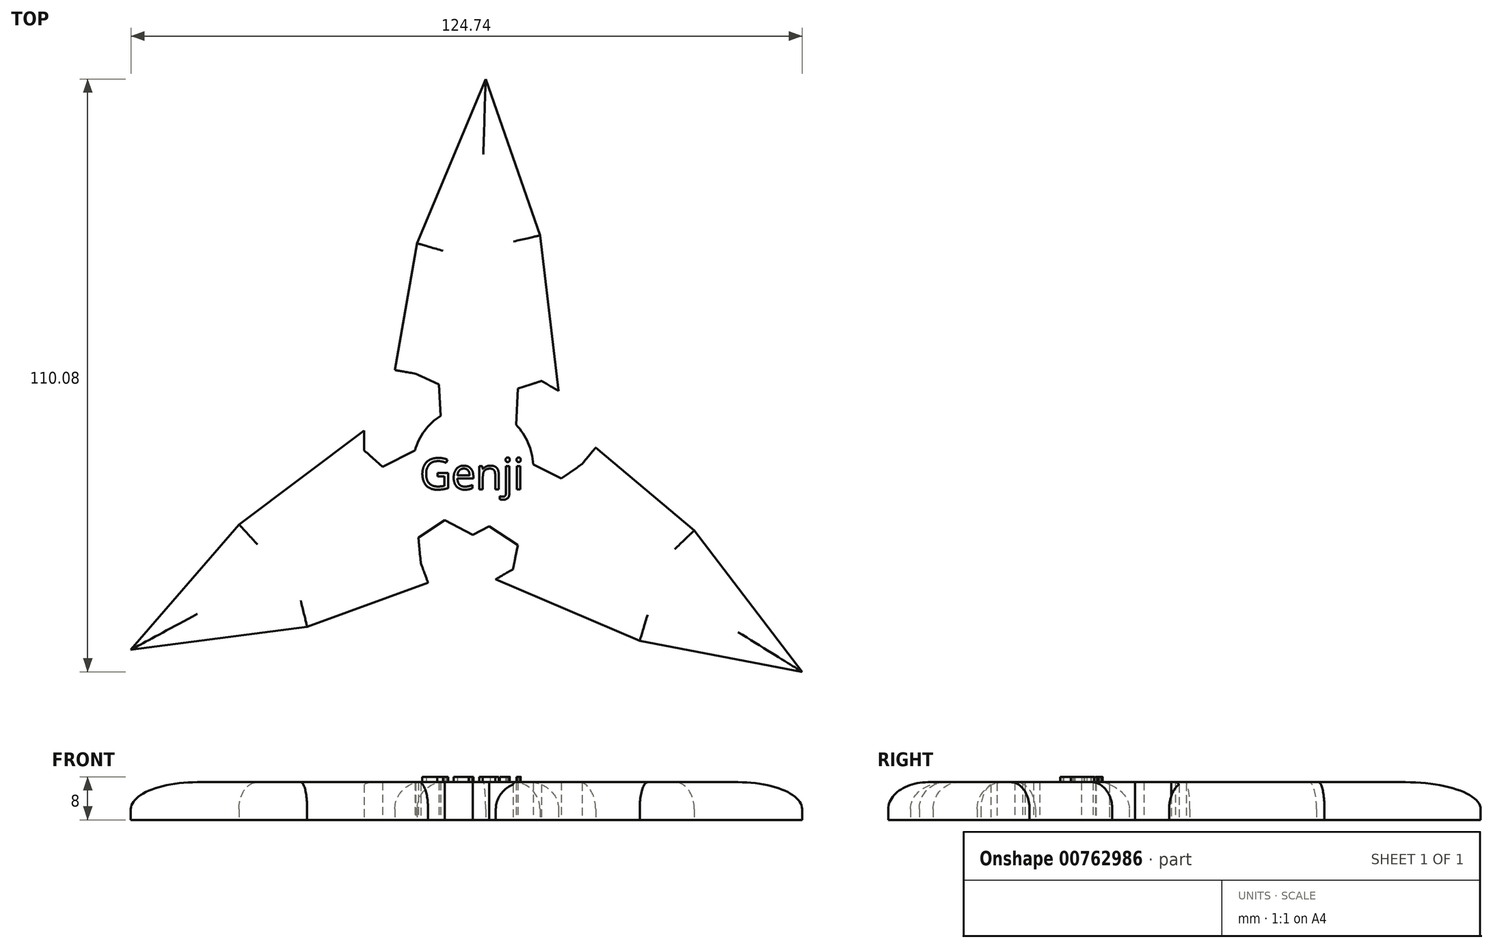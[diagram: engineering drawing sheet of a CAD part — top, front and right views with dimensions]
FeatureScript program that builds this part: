
annotation { "Feature Type Name" : "Feature", "Feature Type Description" : "" }
export const myFeature = defineFeature(function(context is Context, id is Id, definition is map)
    precondition{}
    {
        {
            var Q0;
            Q0=qCreatedBy(makeId("Top.planeOp"),FACE);
            var sketch = newSketch(context, id + "F0", { "sketchPlane" : qUnion([Q0])});
            skCircle(sketch, "E0", {"center": v(0, 0) * mm, "radius": 11.2 * mm});
            skLineSegment(sketch, "E1", {"start": v(-7.42, 8.39) * mm, "end": v(-10.77, 3.06) * mm});
            skLineSegment(sketch, "E2", {"start": v(-10.77, 3.06) * mm, "end": v(-16.78, 0) * mm});
            skLineSegment(sketch, "E3", {"start": v(-16.78, 0) * mm, "end": v(-20.2, 3.06) * mm});
            skLineSegment(sketch, "E4", {"start": v(-20.2, 3.06) * mm, "end": v(-20.2, 6.74) * mm});
            skLineSegment(sketch, "E5", {"start": v(-20.2, 6.74) * mm, "end": v(-43.47, -10.7) * mm});
            skLineSegment(sketch, "E6", {"start": v(-43.47, -10.7) * mm, "end": v(-63.55, -33.96) * mm});
            skLineSegment(sketch, "E7", {"start": v(-63.55, -33.96) * mm, "end": v(-30.79, -29.73) * mm});
            skLineSegment(sketch, "E8", {"start": v(-30.79, -29.73) * mm, "end": v(-8.32, -21.54) * mm});
            skLineSegment(sketch, "E9", {"start": v(-8.32, -21.54) * mm, "end": v(-9.67, -17.85) * mm});
            skLineSegment(sketch, "E10", {"start": v(-9.67, -17.85) * mm, "end": v(-10.09, -13.12) * mm});
            skLineSegment(sketch, "E11", {"start": v(-10.09, -13.12) * mm, "end": v(-5.2, -9.92) * mm});
            skLineSegment(sketch, "E12", {"start": v(-5.2, -9.92) * mm, "end": v(0, -12.64) * mm});
            skLineSegment(sketch, "E13", {"start": v(0, -12.64) * mm, "end": v(5.2, -9.92) * mm});
            skLineSegment(sketch, "E14.1.0", {"start": v(4.26, -20.86) * mm, "end": v(31, -32.3) * mm});
            skLineSegment(sketch, "E14.1.1", {"start": v(31, -32.3) * mm, "end": v(61.19, -38.06) * mm});
            skLineSegment(sketch, "E14.1.2", {"start": v(61.19, -38.06) * mm, "end": v(41.14, -11.8) * mm});
            skLineSegment(sketch, "E14.1.3", {"start": v(41.14, -11.8) * mm, "end": v(22.81, 3.56) * mm});
            skLineSegment(sketch, "E14.1.4", {"start": v(22.81, 3.56) * mm, "end": v(20.3, 0.55) * mm});
            skLineSegment(sketch, "E14.1.5", {"start": v(20.3, 0.55) * mm, "end": v(16.4, -2.18) * mm});
            skLineSegment(sketch, "E14.1.6", {"start": v(16.4, -2.18) * mm, "end": v(11.2, 0.46) * mm});
            skLineSegment(sketch, "E14.1.7", {"start": v(7.45, -19.02) * mm, "end": v(4.26, -20.86) * mm});
            skLineSegment(sketch, "E14.1.8", {"start": v(8.4, -14.53) * mm, "end": v(7.45, -19.02) * mm});
            skLineSegment(sketch, "E14.1.9", {"start": v(2.74, -10.86) * mm, "end": v(8.4, -14.53) * mm});
            skLineSegment(sketch, "E14.2.0", {"start": v(15.93, 14.12) * mm, "end": v(12.47, 43) * mm});
            skLineSegment(sketch, "E14.2.1", {"start": v(12.47, 43) * mm, "end": v(2.37, 72.02) * mm});
            skLineSegment(sketch, "E14.2.2", {"start": v(2.37, 72.02) * mm, "end": v(-10.35, 41.53) * mm});
            skLineSegment(sketch, "E14.2.3", {"start": v(-10.35, 41.53) * mm, "end": v(-14.49, 17.98) * mm});
            skLineSegment(sketch, "E14.2.4", {"start": v(-14.49, 17.98) * mm, "end": v(-10.62, 17.3) * mm});
            skLineSegment(sketch, "E14.2.5", {"start": v(-10.62, 17.3) * mm, "end": v(-6.32, 15.3) * mm});
            skLineSegment(sketch, "E14.2.6", {"start": v(-6.32, 15.3) * mm, "end": v(-6, 9.46) * mm});
            skLineSegment(sketch, "E14.2.7", {"start": v(12.74, 15.96) * mm, "end": v(15.93, 14.12) * mm});
            skLineSegment(sketch, "E14.2.8", {"start": v(8.4, 14.53) * mm, "end": v(12.74, 15.96) * mm});
            skLineSegment(sketch, "E14.2.9", {"start": v(8.04, 7.8) * mm, "end": v(8.4, 14.53) * mm});
            skLineSegment(sketch, "E15", {"start": v(-26.7, 1.86) * mm, "end": v(-29.22, -12.7) * mm});
            skPoint(sketch, "E15.endSnap0", {"position": v(5.56, -12.7) * mm});
            skLineSegment(sketch, "E16", {"start": v(-29.22, -12.7) * mm, "end": v(-13, -23.24) * mm});
            skLineSegment(sketch, "E17", {"start": v(-31.83, -1.98) * mm, "end": v(-57.12, -30.65) * mm});
            skLineSegment(sketch, "E18", {"start": v(-57.12, -30.65) * mm, "end": v(-16.88, -24.66) * mm});
            skLineSegment(sketch, "E19.1.0", {"start": v(17.63, -26.58) * mm, "end": v(55.1, -34.14) * mm});
            skLineSegment(sketch, "E19.1.1", {"start": v(55.1, -34.14) * mm, "end": v(29.8, -2.3) * mm});
            skLineSegment(sketch, "E19.1.2", {"start": v(25.6, -18.95) * mm, "end": v(26.62, 0.37) * mm});
            skLineSegment(sketch, "E19.1.3", {"start": v(11.74, -24.05) * mm, "end": v(25.6, -18.95) * mm});
            skLineSegment(sketch, "E19.2.0", {"start": v(14.2, 28.56) * mm, "end": v(2.01, 64.79) * mm});
            skLineSegment(sketch, "E19.2.1", {"start": v(2.01, 64.79) * mm, "end": v(-12.91, 26.95) * mm});
            skLineSegment(sketch, "E19.2.2", {"start": v(3.61, 31.65) * mm, "end": v(-13.63, 22.87) * mm});
            skLineSegment(sketch, "E19.2.3", {"start": v(14.96, 22.2) * mm, "end": v(3.61, 31.65) * mm});
            skLineSegment(sketch, "E20", {"start": v(8.04, 7.8) * mm, "end": v(11.2, 0.46) * mm});
            skSolve(sketch);
        }
        {
            var Q0;
            Q0 = qSketchRegion(id + "F0", true);
            extrude(context, id + "F1", {"entities" : qUnion([Q0]), "depth" : 7 * mm, "offsetDistance" : 25 * mm});
        }
        {
            var Q0;
            Q0=makeQuery(id+"F1.opExtrude","CAP_EDGE",EDGE,{"disambiguationData":[OSD([sQuery(id+"F0.wireOp",EDGE,"E14.2.3")])],"isStart":false});
            var Q1;
            Q1=makeQuery(id+"F1.opExtrude","CAP_EDGE",EDGE,{"disambiguationData":[OSD([sQuery(id+"F0.wireOp",EDGE,"E14.2.2")])],"isStart":false});
            var Q2;
            Q2=makeQuery(id+"F1.opExtrude","CAP_EDGE",EDGE,{"disambiguationData":[OSD([sQuery(id+"F0.wireOp",EDGE,"E14.2.0")])],"isStart":false});
            var Q3;
            Q3=makeQuery(id+"F1.opExtrude","CAP_EDGE",EDGE,{"disambiguationData":[OSD([sQuery(id+"F0.wireOp",EDGE,"E14.2.1")])],"isStart":false});
            var Q4;
            Q4=makeQuery(id+"F1.opExtrude","CAP_EDGE",EDGE,{"disambiguationData":[OSD([sQuery(id+"F0.wireOp",EDGE,"E5")])],"isStart":false});
            var Q5;
            Q5=makeQuery(id+"F1.opExtrude","CAP_EDGE",EDGE,{"disambiguationData":[OSD([sQuery(id+"F0.wireOp",EDGE,"E6")])],"isStart":false});
            var Q6;
            Q6=makeQuery(id+"F1.opExtrude","CAP_EDGE",EDGE,{"disambiguationData":[OSD([sQuery(id+"F0.wireOp",EDGE,"E14.1.0")])],"isStart":false});
            var Q7;
            Q7=makeQuery(id+"F1.opExtrude","CAP_EDGE",EDGE,{"disambiguationData":[OSD([sQuery(id+"F0.wireOp",EDGE,"E14.1.1")])],"isStart":false});
            var Q8;
            Q8=makeQuery(id+"F1.opExtrude","CAP_EDGE",EDGE,{"disambiguationData":[OSD([sQuery(id+"F0.wireOp",EDGE,"E14.1.3")])],"isStart":false});
            var Q9;
            Q9=makeQuery(id+"F1.opExtrude","CAP_EDGE",EDGE,{"disambiguationData":[OSD([sQuery(id+"F0.wireOp",EDGE,"E14.1.2")])],"isStart":false});
            var Q10;
            Q10=makeQuery(id+"F1.opExtrude","CAP_EDGE",EDGE,{"disambiguationData":[OSD([sQuery(id+"F0.wireOp",EDGE,"E7")])],"isStart":false});
            var Q11;
            Q11=makeQuery(id+"F1.opExtrude","CAP_EDGE",EDGE,{"disambiguationData":[OSD([sQuery(id+"F0.wireOp",EDGE,"E8")])],"isStart":false});
            fillet(context, id + "F2", {"entities" : qUnion([Q0, Q1, Q2, Q3, Q4, Q5, Q6, Q7, Q8, Q9, Q10, Q11]), "radius" : 5 * mm, "tangentPropagation" : true, "allowEdgeOverflow" : false});
        }
        {
            var Q0;
            Q0=makeQuery(id+"F1.opExtrude","CAP_FACE",FACE,{"disambiguationData":[OSD([sQuery(id+"F0.wireOp",EDGE,"E0"),sQuery(id+"F0.wireOp",EDGE,"E2"),sQuery(id+"F0.wireOp",EDGE,"E3"),sQuery(id+"F0.wireOp",EDGE,"E4"),sQuery(id+"F0.wireOp",EDGE,"E5"),sQuery(id+"F0.wireOp",EDGE,"E6"),sQuery(id+"F0.wireOp",EDGE,"E7"),sQuery(id+"F0.wireOp",EDGE,"E8"),sQuery(id+"F0.wireOp",EDGE,"E9"),sQuery(id+"F0.wireOp",EDGE,"E10"),sQuery(id+"F0.wireOp",EDGE,"E11"),sQuery(id+"F0.wireOp",EDGE,"E12"),sQuery(id+"F0.wireOp",EDGE,"E13"),sQuery(id+"F0.wireOp",EDGE,"E14.1.0"),sQuery(id+"F0.wireOp",EDGE,"E14.1.1"),sQuery(id+"F0.wireOp",EDGE,"E14.1.2"),sQuery(id+"F0.wireOp",EDGE,"E14.1.3"),sQuery(id+"F0.wireOp",EDGE,"E14.1.4"),sQuery(id+"F0.wireOp",EDGE,"E14.1.5"),sQuery(id+"F0.wireOp",EDGE,"E14.1.6"),sQuery(id+"F0.wireOp",EDGE,"E14.1.7"),sQuery(id+"F0.wireOp",EDGE,"E14.1.8"),sQuery(id+"F0.wireOp",EDGE,"E14.1.9"),sQuery(id+"F0.wireOp",EDGE,"E14.2.0"),sQuery(id+"F0.wireOp",EDGE,"E14.2.1"),sQuery(id+"F0.wireOp",EDGE,"E14.2.2"),sQuery(id+"F0.wireOp",EDGE,"E14.2.3"),sQuery(id+"F0.wireOp",EDGE,"E14.2.4"),sQuery(id+"F0.wireOp",EDGE,"E14.2.5"),sQuery(id+"F0.wireOp",EDGE,"E14.2.6"),sQuery(id+"F0.wireOp",EDGE,"E14.2.7"),sQuery(id+"F0.wireOp",EDGE,"E14.2.8"),sQuery(id+"F0.wireOp",EDGE,"E14.2.9")])],"isStart":false});
            var sketch = newSketch(context, id + "F3", { "sketchPlane" : qUnion([Q0])});
            skText(sketch, "E21", { "text": "Genji\n", "fontName": "OpenSans-Regular.ttf"});
            const initialGuessF3  = {"E21": [-0.00988, -0.00416, 1, 0, 0.0058]};
            skSetInitialGuess(sketch, initialGuessF3);
            skSolve(sketch);
        }
        {
            var Q0;
            Q0 = qSketchRegion(id + "F3", true);
            extrude(context, id + "F4", {"entities" : qUnion([Q0]), "operationType" : NewBodyOperationType.ADD, "depth" : 1 * mm, "offsetDistance" : 25 * mm});
        }
    });
